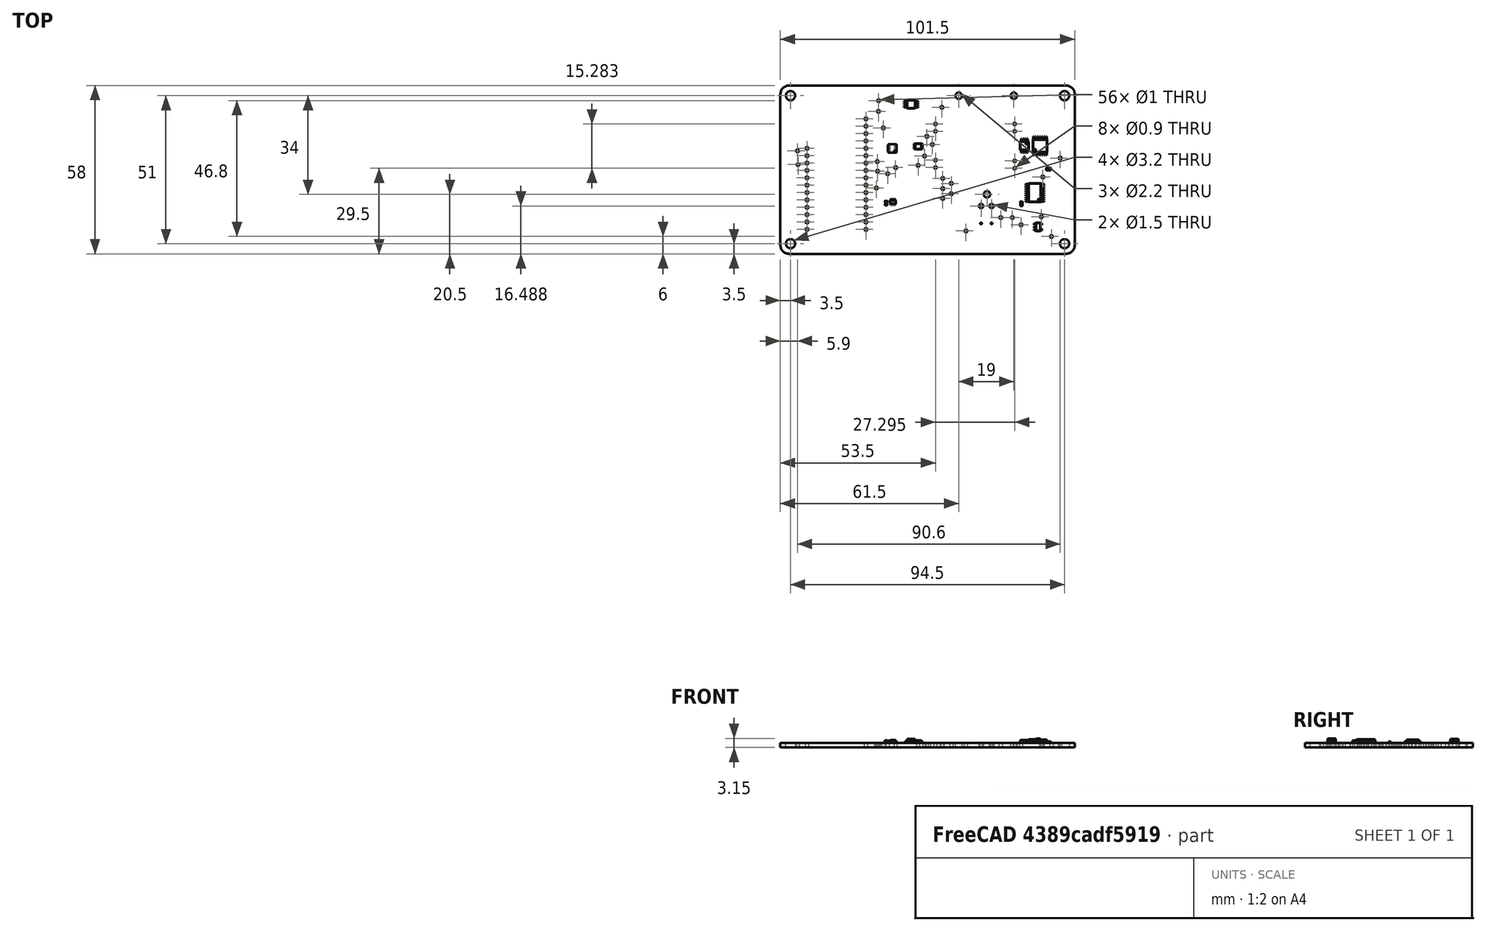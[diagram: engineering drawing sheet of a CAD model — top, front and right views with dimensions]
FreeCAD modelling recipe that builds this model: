
FCSTD DOCUMENT  (FreeCAD 1.0R38641 +678 (Git))
Label: phoenix-pcb-v1.0.1-tsunami
License: All rights reserved
LicenseURL: https://en.wikipedia.org/wiki/All_rights_reserved
objects: App::Link×42, Part::Feature×12, App::Part×4, Sketcher::SketchObject×1
note: 14 computed .brp shape members not serialized (recipe doc carries the construction recipe); baked Part::Feature solids carry a one-line shape summary decoded from their .brp

FEATURE [Part::Feature] Pcb_bfa0
  Placement = pos=(-30,20,0) rot=(0,0,1;0rad)
  shape: bbox 101.5 x 58 x 1.6 mm, 85 faces (baked)
FEATURE [Sketcher::SketchObject] PCB_Sketch_bfa0
  ArcFitTolerance = 1e-06
  FullyConstrained = false
  MakeInternals = false
  sketch-geometry (8):
    g0: LineSegment StartX=3 StartY=0 StartZ=0 EndX=98.5 EndY=-3.1e-15 EndZ=0
    g1: LineSegment StartX=101.5 StartY=-3 StartZ=0 EndX=101.5 EndY=-55 EndZ=0
    g2: LineSegment StartX=-9e-16 StartY=-55 StartZ=0 EndX=-4e-16 EndY=-3 EndZ=0
    g3: LineSegment StartX=98.5 StartY=-58 StartZ=0 EndX=3 EndY=-58 EndZ=0
    g4: ArcOfCircle CenterX=98.5 CenterY=-55 CenterZ=0 NormalX=0 NormalY=0 NormalZ=-1 AngleXU=-3.14159 Radius=3 StartAngle=0 EndAngle=1.5708
    g5: ArcOfCircle CenterX=3 CenterY=-3 CenterZ=0 NormalX=0 NormalY=0 NormalZ=-1 AngleXU=3.90995e-07 Radius=3 StartAngle=0 EndAngle=1.5708
    g6: ArcOfCircle CenterX=3 CenterY=-55 CenterZ=0 NormalX=0 NormalY=0 NormalZ=-1 AngleXU=-1.5708 Radius=3 StartAngle=0 EndAngle=1.5708
    g7: ArcOfCircle CenterX=98.5 CenterY=-3 CenterZ=0 NormalX=0 NormalY=0 NormalZ=-1 AngleXU=1.5708 Radius=3 StartAngle=0 EndAngle=1.5708
  constraints (8):
    c: Coincident(g2,g6)
    c: Coincident(g2,g5)
    c: Coincident(g3,g6)
    c: Coincident(g0,g5)
    c: Coincident(g3,g4)
    c: Coincident(g0,g7)
    c: Coincident(g1,g4)
    c: Coincident(g1,g7)
FEATURE [App::Part] Board_Geoms_bfa0
  Group = -> [Pcb_bfa0,PCB_Sketch_bfa0]
  Origin = -> Origin
FEATURE [Part::Feature] Shape  label="R19_R_0603_1608Metric_e81c35781ce5"
  Placement = pos=(92.475,-28.7599,0) rot=(0,0,1;0rad)
  shape: bbox 1.6 x 0.8 x 0.45 mm, 26 faces (baked)
FEATURE [App::Link] R19_R_0603_1608Metric_e81c35781ce5_ln_  label="R7_R_0603_1608Metric_df876850ed1e"
  LinkPlacement = pos=(79.275,-40.2599,0) rot=(0,0,1;0rad)
  LinkedObject = -> Shape
  Placement = pos=(79.275,-40.2599,0) rot=(0,0,1;0rad)
FEATURE [Part::Feature] Shape001  label="C12_C_0603_1608Metric_43dd25189e75"
  Placement = pos=(83.1,-40.775,0) rot=(0,0,-1;1.5708rad)
  shape: bbox 0.8 x 1.6 x 0.8 mm, 28 faces (baked)
FEATURE [App::Link] C12_C_0603_1608Metric_43dd25189e75_ln_  label="C5_C_0603_1608Metric_e1bb111b0e8a"
  LinkPlacement = pos=(49.8145,-5.55904,0) rot=(0,0,1;0rad)
  LinkedObject = -> Shape001
  Placement = pos=(49.8145,-5.55904,0) rot=(0,0,1;0rad)
FEATURE [Part::Feature] Shape002  label="U1_VSSOP-8_3x3mm_P0.65mm_b0bd8732d9d8"
  Placement = pos=(45.0875,-6.425,0) rot=(0,0,1;0rad)
  shape: bbox 4.9 x 3 x 1.35 mm, 147 faces (baked)
FEATURE [Part::Feature] Shape003  label="U7_MSOP_8_3x3mm_P065mm_0b8d5e192aae"
  Placement = pos=(84.125,-20.7287,0) rot=(0,0,-1;1.5708rad)
  shape: bbox 3 x 4.9 x 0.95 mm, 156 faces (baked)
FEATURE [App::Link] C12_C_0603_1608Metric_43dd25189e75_ln_001  label="C18_C_0603_1608Metric_cf3f1f72a176"
  LinkPlacement = pos=(95.875,-19.7599,0) rot=(0,0,1;3.14159rad)
  LinkedObject = -> Shape001
  Placement = pos=(95.875,-19.7599,0) rot=(0,0,1;3.14159rad)
FEATURE [App::Link] C12_C_0603_1608Metric_43dd25189e75_ln_002  label="C7_C_0603_1608Metric_5fe292424d0b"
  LinkPlacement = pos=(49.0629,-7.83495,0) rot=(0,0,-1;1.5708rad)
  LinkedObject = -> Shape001
  Placement = pos=(49.0629,-7.83495,0) rot=(0,0,-1;1.5708rad)
FEATURE [App::Link] C12_C_0603_1608Metric_43dd25189e75_ln_003  label="C6_C_0603_1608Metric_6f7ce299bd57"
  LinkPlacement = pos=(39.475,-8.325,0) rot=(0,0,-1;1.5708rad)
  LinkedObject = -> Shape001
  Placement = pos=(39.475,-8.325,0) rot=(0,0,-1;1.5708rad)
FEATURE [App::Link] R19_R_0603_1608Metric_e81c35781ce5_ln_001  label="R2_R_0603_1608Metric_bdd129e940a4"
  LinkPlacement = pos=(50.675,-27,0) rot=(0,0,1;3.14159rad)
  LinkedObject = -> Shape
  Placement = pos=(50.675,-27,0) rot=(0,0,1;3.14159rad)
FEATURE [App::Link] R19_R_0603_1608Metric_e81c35781ce5_ln_002  label="Rset1_R_0603_1608Metric_0a43983b202c"
  LinkPlacement = pos=(42.825,-20.75,0) rot=(0,0,1;3.14159rad)
  LinkedObject = -> Shape
  Placement = pos=(42.825,-20.75,0) rot=(0,0,1;3.14159rad)
FEATURE [Part::Feature] Shape005  label="U2_DFN-8-1EP_3x3mm_Pitch0.5mm_9c5140f70b24"
  Placement = pos=(38.585,-21.655,0) rot=(0,0,1;3.14159rad)
  shape: bbox 3 x 2.98 x 0.77 mm, 62 faces (baked)
FEATURE [App::Link] C12_C_0603_1608Metric_43dd25189e75_ln_004  label="C13_C_0603_1608Metric_2d995ea0f250"
  LinkPlacement = pos=(81.6,-40.775,0) rot=(0,0,-1;1.5708rad)
  LinkedObject = -> Shape001
  Placement = pos=(81.6,-40.775,0) rot=(0,0,-1;1.5708rad)
FEATURE [App::Link] R19_R_0603_1608Metric_e81c35781ce5_ln_003  label="R5_R_0603_1608Metric_04dba9f839b4"
  LinkPlacement = pos=(80.6,-22.2599,0) rot=(0,0,1;3.14159rad)
  LinkedObject = -> Shape
  Placement = pos=(80.6,-22.2599,0) rot=(0,0,1;3.14159rad)
FEATURE [App::Link] C12_C_0603_1608Metric_43dd25189e75_ln_005  label="C16_C_0603_1608Metric_2a5a0c6a626c"
  LinkPlacement = pos=(92.375,-41.2599,0) rot=(0,0,1;0rad)
  LinkedObject = -> Shape001
  Placement = pos=(92.375,-41.2599,0) rot=(0,0,1;0rad)
FEATURE [App::Link] R19_R_0603_1608Metric_e81c35781ce5_ln_004  label="RFB2_R_0603_1608Metric_fa4530d1918e"
  LinkPlacement = pos=(85.575,-25.7,0) rot=(0,0,1;0rad)
  LinkedObject = -> Shape
  Placement = pos=(85.575,-25.7,0) rot=(0,0,1;0rad)
FEATURE [App::Link] C12_C_0603_1608Metric_43dd25189e75_ln_006  label="C9_C_0603_1608Metric_6faa5609496b"
  LinkPlacement = pos=(50.7242,-7.875,0) rot=(0,0,-1;1.5708rad)
  LinkedObject = -> Shape001
  Placement = pos=(50.7242,-7.875,0) rot=(0,0,-1;1.5708rad)
FEATURE [App::Link] C12_C_0603_1608Metric_43dd25189e75_ln_007  label="C11_C_0603_1608Metric_2912fba1d5fa"
  LinkPlacement = pos=(92,-48.2788,0) rot=(0,0,-1;1.5708rad)
  LinkedObject = -> Shape001
  Placement = pos=(92,-48.2788,0) rot=(0,0,-1;1.5708rad)
FEATURE [Part::Feature] Shape006  label="U5_VSSOP_8_23x2mm_P05mm_af9a6c2f9d9d"
  Placement = pos=(47.6,-21,0) rot=(0,0,1;3.14159rad)
  shape: bbox 3.1 x 2 x 0.85 mm, 156 faces (baked)
FEATURE [App::Link] R19_R_0603_1608Metric_e81c35781ce5_ln_005  label="R3_R_0603_1608Metric_ae32d66b5177"
  LinkPlacement = pos=(50.175,-13.5,0) rot=(0,0,1;3.14159rad)
  LinkedObject = -> Shape
  Placement = pos=(50.175,-13.5,0) rot=(0,0,1;3.14159rad)
FEATURE [Part::Feature] Shape007  label="U9_TSSOP_20_44x65mm_P065mm_1748040f196b"
  Placement = pos=(87.7375,-36.9349,0) rot=(0,0,1;3.14159rad)
  shape: bbox 6.4 x 6.5 x 1.2 mm, 336 faces (baked)
FEATURE [App::Link] R19_R_0603_1608Metric_e81c35781ce5_ln_006  label="R8_R_0603_1608Metric_02c9f0a1c546"
  LinkPlacement = pos=(79.275,-38.7599,0) rot=(0,0,1;0rad)
  LinkedObject = -> Shape
  Placement = pos=(79.275,-38.7599,0) rot=(0,0,1;0rad)
FEATURE [App::Link] R19_R_0603_1608Metric_e81c35781ce5_ln_007  label="TH1_R_0603_1608Metric_4b5df4f6c50b"
  LinkPlacement = pos=(75.59,-48.925,0) rot=(0,0,-1;1.5708rad)
  LinkedObject = -> Shape
  Placement = pos=(75.59,-48.925,0) rot=(0,0,-1;1.5708rad)
FEATURE [App::Link] R19_R_0603_1608Metric_e81c35781ce5_ln_008  label="RFB1_R_0603_1608Metric_a867aa814863"
  LinkPlacement = pos=(86.1875,-15.9037,0) rot=(0,0,1;0rad)
  LinkedObject = -> Shape
  Placement = pos=(86.1875,-15.9037,0) rot=(0,0,1;0rad)
FEATURE [App::Link] C12_C_0603_1608Metric_43dd25189e75_ln_008  label="C2_C_0603_1608Metric_ffe2bc87c12a"
  LinkPlacement = pos=(45.1858,-3.83244,0) rot=(0,0,1;0rad)
  LinkedObject = -> Shape001
  Placement = pos=(45.1858,-3.83244,0) rot=(0,0,1;0rad)
FEATURE [App::Link] C12_C_0603_1608Metric_43dd25189e75_ln_009  label="C14_C_0603_1608Metric_45402db31f73"
  LinkPlacement = pos=(93.125,-38.3,0) rot=(0,0,1;0rad)
  LinkedObject = -> Shape001
  Placement = pos=(93.125,-38.3,0) rot=(0,0,1;0rad)
FEATURE [App::Link] R19_R_0603_1608Metric_e81c35781ce5_ln_009  label="R14_R_0603_1608Metric_45fedd258f38"
  LinkPlacement = pos=(78.99,-48.925,0) rot=(0,0,1;1.5708rad)
  LinkedObject = -> Shape
  Placement = pos=(78.99,-48.925,0) rot=(0,0,1;1.5708rad)
FEATURE [App::Link] R19_R_0603_1608Metric_e81c35781ce5_ln_010  label="R10_R_0603_1608Metric_8ec42b163691"
  LinkPlacement = pos=(79.275,-35.7599,0) rot=(0,0,1;0rad)
  LinkedObject = -> Shape
  Placement = pos=(79.275,-35.7599,0) rot=(0,0,1;0rad)
FEATURE [App::Link] R19_R_0603_1608Metric_e81c35781ce5_ln_011  label="R18_R_0603_1608Metric_ee66729e9e05"
  LinkPlacement = pos=(72.7879,-49.6484,0) rot=(0,0,1;3.14159rad)
  LinkedObject = -> Shape
  Placement = pos=(72.7879,-49.6484,0) rot=(0,0,1;3.14159rad)
FEATURE [App::Link] C12_C_0603_1608Metric_43dd25189e75_ln_010  label="C15_C_0603_1608Metric_d5b246a7317c"
  LinkPlacement = pos=(92.825,-42.7599,0) rot=(0,0,1;0rad)
  LinkedObject = -> Shape001
  Placement = pos=(92.825,-42.7599,0) rot=(0,0,1;0rad)
FEATURE [App::Link] C12_C_0603_1608Metric_43dd25189e75_ln_011  label="C8_C_0603_1608Metric_9caa440274d4"
  LinkPlacement = pos=(40.7255,-37.7255,0) rot=(0,0,1;0rad)
  LinkedObject = -> Shape001
  Placement = pos=(40.7255,-37.7255,0) rot=(0,0,1;0rad)
FEATURE [App::Link] R19_R_0603_1608Metric_e81c35781ce5_ln_012  label="R11_R_0603_1608Metric_a362d15d1ace"
  LinkPlacement = pos=(79.275,-34.2599,0) rot=(0,0,1;0rad)
  LinkedObject = -> Shape
  Placement = pos=(79.275,-34.2599,0) rot=(0,0,1;0rad)
FEATURE [App::Link] R19_R_0603_1608Metric_e81c35781ce5_ln_013  label="R12_R_0603_1608Metric_e843cbb940e9"
  LinkPlacement = pos=(79.275,-32.7599,0) rot=(0,0,1;0rad)
  LinkedObject = -> Shape
  Placement = pos=(79.275,-32.7599,0) rot=(0,0,1;0rad)
FEATURE [Part::Feature] Shape008  label="L1_L_0603_1608Metric_6e4b57586c89"
  Placement = pos=(36.4505,-40.513,0) rot=(0,0,1;1.5708rad)
  shape: bbox 0.8 x 1.6 x 0.8 mm, 28 faces (baked)
FEATURE [App::Link] C12_C_0603_1608Metric_43dd25189e75_ln_012  label="C10_C_0603_1608Metric_0caffe4b230c"
  LinkPlacement = pos=(85.8,-48.3137,0) rot=(0,0,-1;1.5708rad)
  LinkedObject = -> Shape001
  Placement = pos=(85.8,-48.3137,0) rot=(0,0,-1;1.5708rad)
FEATURE [App::Link] R19_R_0603_1608Metric_e81c35781ce5_ln_014  label="R20_R_0603_1608Metric_bd504c419ae9"
  LinkPlacement = pos=(95.775,-18.2599,0) rot=(0,0,1;3.14159rad)
  LinkedObject = -> Shape
  Placement = pos=(95.775,-18.2599,0) rot=(0,0,1;3.14159rad)
FEATURE [App::Link] R19_R_0603_1608Metric_e81c35781ce5_ln_015  label="R17_R_0603_1608Metric_f07c92bcc6ee"
  LinkPlacement = pos=(77.19,-48.925,0) rot=(0,0,1;1.5708rad)
  LinkedObject = -> Shape
  Placement = pos=(77.19,-48.925,0) rot=(0,0,1;1.5708rad)
FEATURE [App::Link] R19_R_0603_1608Metric_e81c35781ce5_ln_016  label="Rout1_R_0603_1608Metric_3044a5c279e2"
  LinkPlacement = pos=(42.825,-22.25,0) rot=(0,0,1;3.14159rad)
  LinkedObject = -> Shape
  Placement = pos=(42.825,-22.25,0) rot=(0,0,1;3.14159rad)
FEATURE [App::Link] C12_C_0603_1608Metric_43dd25189e75_ln_013  label="C3_C_0603_1608Metric_40e8dbfff7af"
  LinkPlacement = pos=(38.8755,-44.0755,0) rot=(0,0,1;0rad)
  LinkedObject = -> Shape001
  Placement = pos=(38.8755,-44.0755,0) rot=(0,0,1;0rad)
FEATURE [Part::Feature] Shape009  label="U3_SOT_363_SC_70_6_2b77724525eb"
  Placement = pos=(38.8005,-40.1255,0) rot=(0,0,1;1.5708rad)
  shape: bbox 2 x 2 x 1.05 mm, 118 faces (baked)
FEATURE [App::Link] R19_R_0603_1608Metric_e81c35781ce5_ln_017  label="R13_R_0603_1608Metric_49b6a3b2dfdc"
  LinkPlacement = pos=(79.275,-41.7599,0) rot=(0,0,1;0rad)
  LinkedObject = -> Shape
  Placement = pos=(79.275,-41.7599,0) rot=(0,0,1;0rad)
FEATURE [App::Link] R19_R_0603_1608Metric_e81c35781ce5_ln_018  label="R4_R_0603_1608Metric_bbc76c5892d3"
  LinkPlacement = pos=(80.4982,-18.4451,0) rot=(0,0,1;3.14159rad)
  LinkedObject = -> Shape
  Placement = pos=(80.4982,-18.4451,0) rot=(0,0,1;3.14159rad)
FEATURE [Part::Feature] Shape011  label="U8_TSSOP_16_44x5mm_P065mm_5ce80917f075"
  Placement = pos=(89.5375,-20.7662,0) rot=(0,0,1;1.5708rad)
  shape: bbox 5 x 6.4 x 1.1 mm, 260 faces (baked)
FEATURE [App::Link] R19_R_0603_1608Metric_e81c35781ce5_ln_019  label="R1_R_0603_1608Metric_013c2982079e"
  LinkPlacement = pos=(47.175,-18.25,0) rot=(0,0,1;3.14159rad)
  LinkedObject = -> Shape
  Placement = pos=(47.175,-18.25,0) rot=(0,0,1;3.14159rad)
FEATURE [Part::Feature] Shape012  label="U6_SOT_23_5_cae0d91c1014"
  Placement = pos=(88.87,-48.7637,0) rot=(0,0,1;0rad)
  shape: bbox 2.8 x 2.9 x 1.55 mm, 109 faces (baked)
FEATURE [App::Link] R19_R_0603_1608Metric_e81c35781ce5_ln_020  label="R15_R_0603_1608Metric_c2b8edb76dc4"
  LinkPlacement = pos=(80.5,-48.925,0) rot=(0,0,-1;1.5708rad)
  LinkedObject = -> Shape
  Placement = pos=(80.5,-48.925,0) rot=(0,0,-1;1.5708rad)
FEATURE [App::Link] C12_C_0603_1608Metric_43dd25189e75_ln_014  label="C1_C_0603_1608Metric_aabbb8dd865d"
  LinkPlacement = pos=(38.8255,-42.5755,0) rot=(0,0,1;0rad)
  LinkedObject = -> Shape001
  Placement = pos=(38.8255,-42.5755,0) rot=(0,0,1;0rad)
FEATURE [App::Link] R19_R_0603_1608Metric_e81c35781ce5_ln_021  label="R16_R_0603_1608Metric_54fdf4ed7c6a"
  LinkPlacement = pos=(89.775,-42.7599,0) rot=(0,0,1;0rad)
  LinkedObject = -> Shape
  Placement = pos=(89.775,-42.7599,0) rot=(0,0,1;0rad)
FEATURE [App::Link] R19_R_0603_1608Metric_e81c35781ce5_ln_022  label="R6_R_0603_1608Metric_41f89ef6f0c9"
  LinkPlacement = pos=(76.5,-39.5849,0) rot=(0,0,1;1.5708rad)
  LinkedObject = -> Shape
  Placement = pos=(76.5,-39.5849,0) rot=(0,0,1;1.5708rad)
FEATURE [App::Link] R19_R_0603_1608Metric_e81c35781ce5_ln_023  label="R9_R_0603_1608Metric_e9602802d778"
  LinkPlacement = pos=(79.275,-37.2599,0) rot=(0,0,1;0rad)
  LinkedObject = -> Shape
  Placement = pos=(79.275,-37.2599,0) rot=(0,0,1;0rad)
FEATURE [App::Link] R19_R_0603_1608Metric_e81c35781ce5_ln_024  label="FB1_R_0603_1608Metric_30314544b1ba"
  LinkPlacement = pos=(52.753,-6.075,0) rot=(0,0,1;1.5708rad)
  LinkedObject = -> Shape
  Placement = pos=(52.753,-6.075,0) rot=(0,0,1;1.5708rad)
FEATURE [App::Link] C12_C_0603_1608Metric_43dd25189e75_ln_015  label="C17_C_0603_1608Metric_9f332281af99"
  LinkPlacement = pos=(90.675,-27.2599,0) rot=(0,0,1;3.14159rad)
  LinkedObject = -> Shape001
  Placement = pos=(90.675,-27.2599,0) rot=(0,0,1;3.14159rad)
FEATURE [App::Link] C12_C_0603_1608Metric_43dd25189e75_ln_016  label="C4_C_0603_1608Metric_842c1dc952ed"
  LinkPlacement = pos=(40.975,-8.325,0) rot=(0,0,-1;1.5708rad)
  LinkedObject = -> Shape001
  Placement = pos=(40.975,-8.325,0) rot=(0,0,-1;1.5708rad)
FEATURE [App::Part] Top_bfa0
  Group = -> [Shape,R19_R_0603_1608Metric_e81c35781ce5_ln_,Shape001,C12_C_0603_1608Metric_43dd25189e75_ln_,Shape002,Shape003,C12_C_0603_1608Metric_43dd25189e75_ln_001,C12_C_0603_1608Metric_43dd25189e75_ln_002,C12_C_0603_1608Metric_43dd25189e75_ln_003,R19_R_0603_1608Metric_e81c35781ce5_ln_001,R19_R_0603_1608Metric_e81c35781ce5_ln_002,Shape005,C12_C_0603_1608Metric_43dd25189e75_ln_004,+40 more]
  Origin = -> Origin003
FEATURE [App::Part] Step_Models_bfa0
  Group = -> [Top_bfa0]
  Origin = -> Origin002
FEATURE [App::Part] Board_bfa0  label="phoenix-main-board"
  Group = -> [Board_Geoms_bfa0,Step_Models_bfa0]
  Origin = -> Origin001
